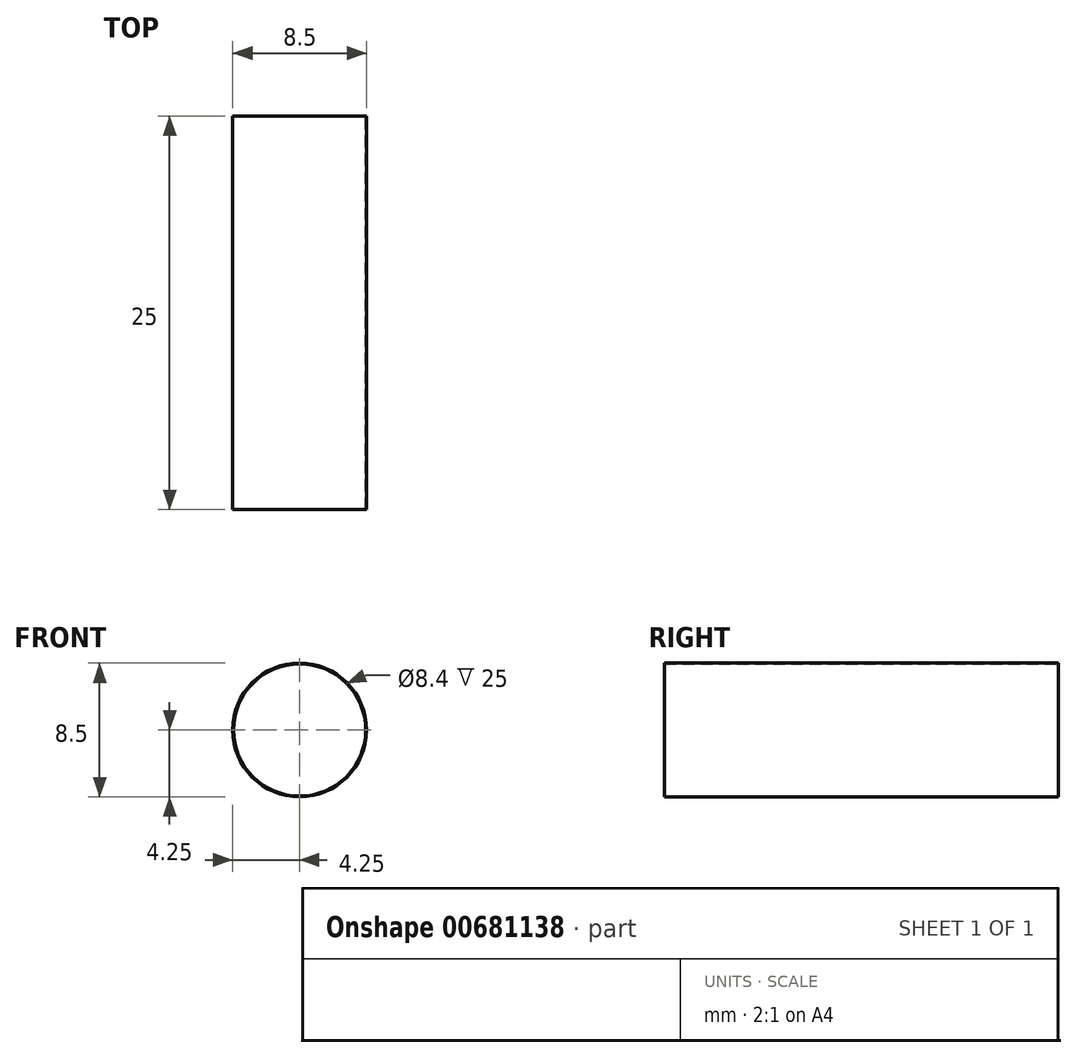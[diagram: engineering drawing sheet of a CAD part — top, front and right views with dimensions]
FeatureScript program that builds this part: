
annotation { "Feature Type Name" : "Feature", "Feature Type Description" : "" }
export const myFeature = defineFeature(function(context is Context, id is Id, definition is map)
    precondition{}
    {
        {
            var Q0;
            Q0=qCreatedBy(makeId("Front.planeOp"),FACE);
            var sketch = newSketch(context, id + "F0", { "sketchPlane" : qUnion([Q0])});
            skCircle(sketch, "E0", {"center": v(0, 0) * mm, "radius": 4.25 * mm});
            skCircle(sketch, "E1", {"center": v(0, 0) * mm, "radius": 4.2 * mm});
            skSolve(sketch);
        }
        {
            var Q0;
            Q0=makeQuery(id+"F0.imprint","IMPRINT",FACE,{"disambiguationData":[TD([[makeQuery(id+"F0.imprint","IMPRINT",EDGE,{"derivedFrom":sQuery(id+"F0.wireOp",EDGE,"E0")}),1.0]])]});
            extrude(context, id + "F1", {"entities" : qUnion([Q0]), "depth" : 25 * mm});
        }
    });
